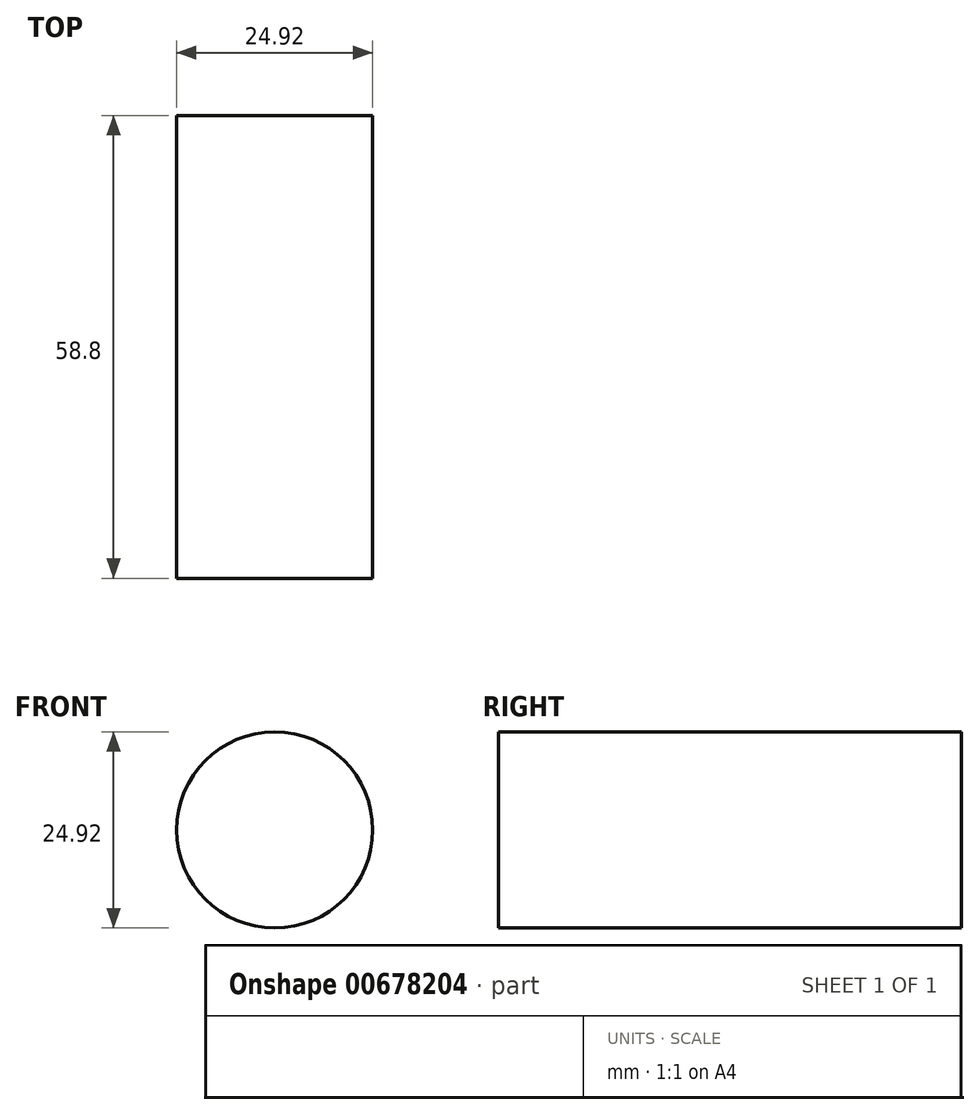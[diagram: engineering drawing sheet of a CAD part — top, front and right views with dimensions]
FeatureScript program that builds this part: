
annotation { "Feature Type Name" : "Feature", "Feature Type Description" : "" }
export const myFeature = defineFeature(function(context is Context, id is Id, definition is map)
    precondition{}
    {
        {
            var Q0;
            Q0=qCreatedBy(makeId("Front.planeOp"),FACE);
            var sketch = newSketch(context, id + "F0", { "sketchPlane" : qUnion([Q0])});
            skCircle(sketch, "E0", {"center": v(0, 0) * mm, "radius": 12.46 * mm});
            skSolve(sketch);
        }
        {
            var Q0;
            Q0 = qSketchRegion(id + "F0", true);
            extrude(context, id + "F1", {"entities" : qUnion([Q0]), "depth" : 58.8 * mm, "offsetDistance" : 25 * mm});
        }
    });
